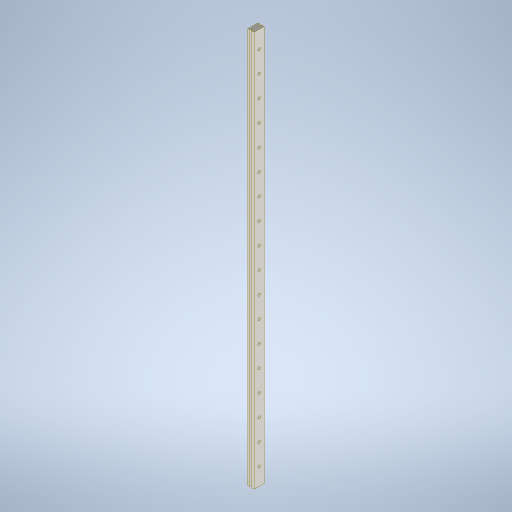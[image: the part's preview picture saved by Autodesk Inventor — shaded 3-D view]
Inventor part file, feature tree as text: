
AUTODESK INVENTOR PART (.ipt)
format: ipt  version: 2023.2 (Build 272271030, 271C)  size: 305,664 bytes
history: native  units: mm
features: sketch x2, other x1, extrude x1, hole x1
ambient origin geometry x8: Origin, YZ Plane, XZ Plane, XY Plane, X Axis, Y Axis, Z Axis, Center Point
bodies: Body1 (feature_tree)
feature tree (5):
  other  "Sólido1"
  extrude  "Extrusão1"  Depth=469.0mm TaperAngle=0.0deg
  hole  "Furo1"  [1 undecoded]
  sketch  "Esboço1"  dims[d0=7.5mm d1=12.0mm d2=8.0mm d3=1.0mm d4=3.5mm d5=0.5mm d6=469.0mm d7=0.0mm]
  sketch  "Esboço2"  dims[d8=190.0mm d10=25.2mm d11=10.0mm d13=10.0mm d15=428.4mm d16=469.0mm d17=20.3mm d18=6.0mm d19=3.0mm d20=13.0mm d21=4.0mm d22=2.0mm d23=90.0deg d24=0.5mm d25=20.594885mm]
note: 1 required parameter value undecoded (feature->parameter linkage not recoverable at this tier; creation-order binding heuristic only, values carry confidence <= 0.55)
